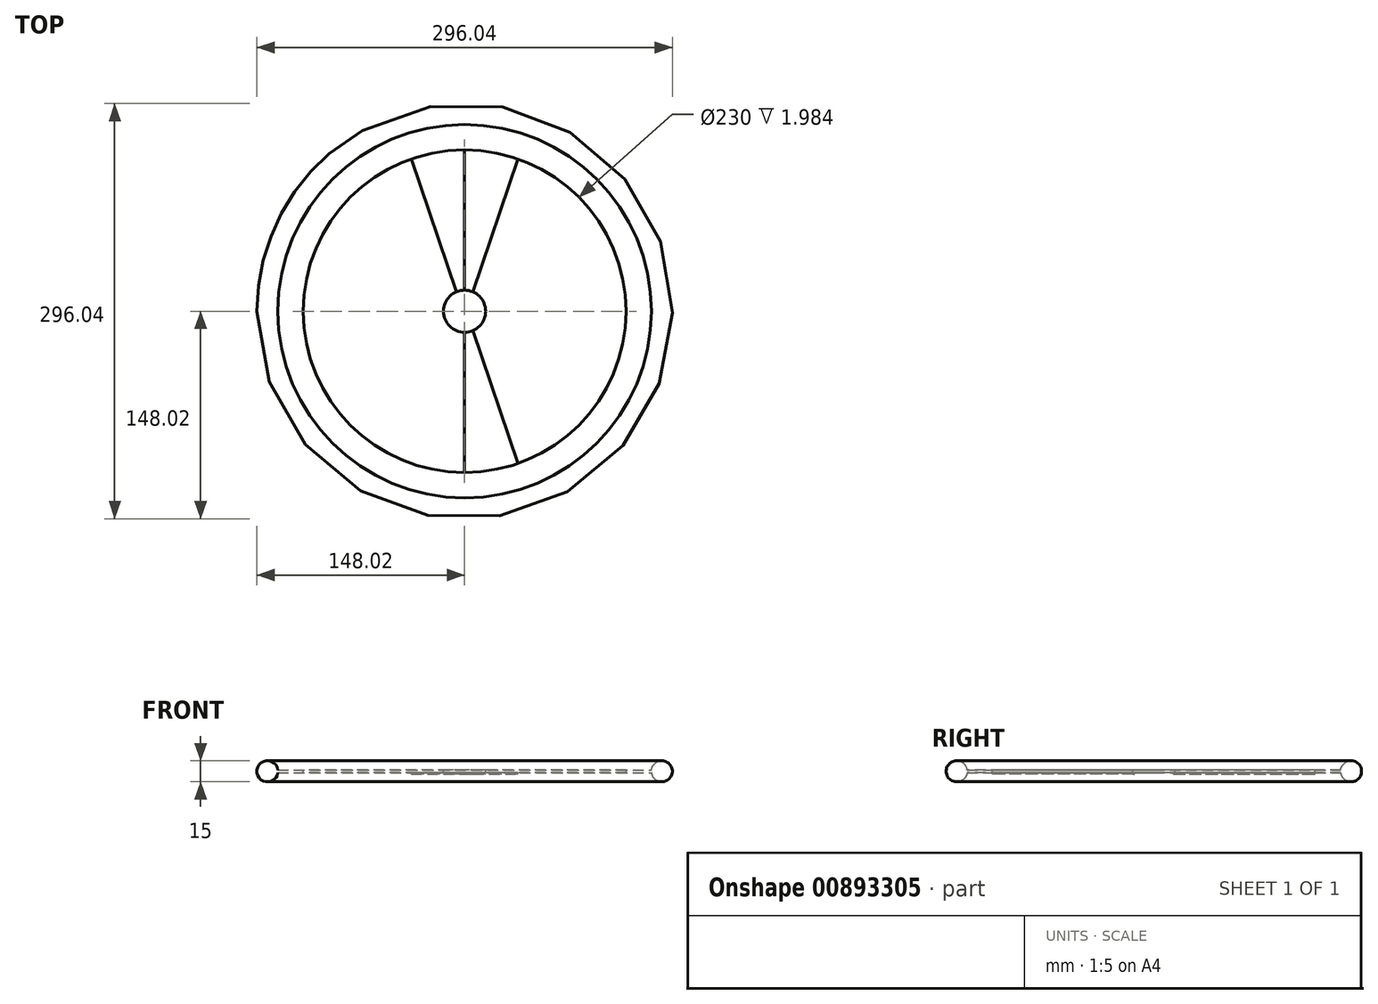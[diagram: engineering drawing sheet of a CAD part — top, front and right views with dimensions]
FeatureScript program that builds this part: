
annotation { "Feature Type Name" : "Feature", "Feature Type Description" : "" }
export const myFeature = defineFeature(function(context is Context, id is Id, definition is map)
    precondition{}
    {
        {
            var Q0;
            Q0=qCreatedBy(makeId("Front.planeOp"),FACE);
            var sketch = newSketch(context, id + "F0", { "sketchPlane" : qUnion([Q0])});
            skCircle(sketch, "E0", {"center": v(140.52, 0) * mm, "radius": 7.5 * mm});
            skPoint(sketch, "E1.0", {"position": v(0, 0) * mm});
            skLineSegment(sketch, "E2", {"start": v(0, 0) * mm, "end": v(140.52, 0) * mm});
            skLineSegment(sketch, "E3", {"start": v(0, 0) * mm, "end": v(0, 62.68) * mm});
            skLineSegment(sketch, "E4.bottom", {"start": v(140.52, -1) * mm, "end": v(0, -1) * mm});
            skLineSegment(sketch, "E4.top", {"start": v(140.52, 1) * mm, "end": v(0, 1) * mm});
            skLineSegment(sketch, "E4.left", {"start": v(140.52, -1) * mm, "end": v(140.52, 1) * mm});
            skLineSegment(sketch, "E4.right", {"start": v(0, -1) * mm, "end": v(0, 1) * mm});
            skPoint(sketch, "E4.middle", {"position": v(70.26, 0) * mm});
            skSolve(sketch);
        }
        {
            var Q0;
            Q0=makeQuery(id+"F0.imprint","IMPRINT",FACE,{"disambiguationData":[TD([[makeQuery(id+"F0.imprint","IMPRINT",EDGE,{"derivedFrom":sQuery(id+"F0.wireOp",EDGE,"E0")}),1.0]])]});
            var Q1;
            {var subQ4=sQuery(id+"F0.wireOp",EDGE,"E0");var subQ6=sQuery(id+"F0.wireOp",EDGE,"E4.top");var subQ8=makeQuery(id+"F0.imprint","INTERSECT",VERTEX,{"derivedFrom":[subQ4,subQ6]});Q1=makeQuery(id+"F0.imprint","IMPRINT",FACE,{"disambiguationData":[TD([[makeQuery(id+"F0.imprint","IMPRINT",EDGE,{"disambiguationData":[TD([[subQ8,1.0]])],"derivedFrom":subQ4}),1.0]])]});}
            var Q2;
            {var subQ0=sQuery(id+"F0.wireOp",EDGE,"E4.top");var subQ1=sQuery(id+"F0.wireOp",EDGE,"E0");var subQ2=makeQuery(id+"F0.imprint","INTERSECT",VERTEX,{"derivedFrom":[subQ1,subQ0]});Q2=makeQuery(id+"F0.imprint","IMPRINT",FACE,{"disambiguationData":[TD([[makeQuery(id+"F0.imprint","IMPRINT",EDGE,{"disambiguationData":[TD([[subQ2,-1.0]])],"derivedFrom":subQ1}),-1.0]])]});}
            var Q3;
            {var subQ0=sQuery(id+"F0.wireOp",EDGE,"E4.bottom");var subQ1=sQuery(id+"F0.wireOp",EDGE,"E0");var subQ2=makeQuery(id+"F0.imprint","INTERSECT",VERTEX,{"derivedFrom":[subQ1,subQ0]});Q3=makeQuery(id+"F0.imprint","IMPRINT",FACE,{"disambiguationData":[TD([[makeQuery(id+"F0.imprint","IMPRINT",EDGE,{"disambiguationData":[TD([[subQ2,1.0]])],"derivedFrom":subQ1}),-1.0]])]});}
            var Q4;
            Q4=sQuery(id+"F0.wireOp",EDGE,"E3");
            revolve(context, id + "F1", {"surfaceOperationType" : NewSurfaceOperationType.NEW, "entities" : qUnion([Q0, Q1, Q2, Q3]), "axis" : qUnion([Q4]), "revolveType" : RevolveType.FULL});
        }
        {
            var Q0;
            Q0=makeQuery(id+"F1.opRevolve","SWEPT_FACE",FACE,{"disambiguationData":[OSD([sQuery(id+"F0.wireOp",EDGE,"E4.top")])]});
            var sketch = newSketch(context, id + "F2", { "sketchPlane" : qUnion([Q0])});
            skCircle(sketch, "E5", {"center": v(0, 0) * mm, "radius": 115 * mm});
            skCircle(sketch, "E6", {"center": v(0, 0) * mm, "radius": 15 * mm});
            skLineSegment(sketch, "E7", {"start": v(-15, 0) * mm, "end": v(-15, -114.02) * mm});
            skLineSegment(sketch, "E8", {"start": v(15, 0) * mm, "end": v(15, -114.02) * mm});
            skSolve(sketch);
        }
        {
            var Q0;
            Q0=makeQuery(id+"F2.imprint","IMPRINT",FACE,{"disambiguationData":[TD([[makeQuery(id+"F2.imprint","IMPRINT",EDGE,{"derivedFrom":sQuery(id+"F2.wireOp",EDGE,"E5")}),1.0]])]});
            extrude(context, id + "F3", {"entities" : qUnion([Q0]), "operationType" : NewBodyOperationType.REMOVE, "oppositeDirection" : true, "depth" : 25 * mm, "offsetDistance" : 25 * mm});
        }
        {
            var Q0;
            Q0=makeQuery(id+"F3.boolean.opBoolean","SPLIT",FACE,{"disambiguationData":[TD([makeQuery(id+"F3.opExtrude","SWEPT_FACE",FACE,{"disambiguationData":[OSD([sQuery(id+"F2.wireOp",EDGE,"E6")])]})])],"derivedFrom":makeQuery(id+"F1.opRevolve","SWEPT_FACE",FACE,{"disambiguationData":[OSD([sQuery(id+"F0.wireOp",EDGE,"E4.bottom")])]})});
            var sketch = newSketch(context, id + "F4", { "sketchPlane" : qUnion([Q0])});
            skCircle(sketch, "E9.0", {"center": v(0, 0) * mm, "radius": 15 * mm});
            skCircle(sketch, "E10.0", {"center": v(0, 0) * mm, "radius": 115 * mm});
            skLineSegment(sketch, "E11", {"start": v(0, 15) * mm, "end": v(0, 115) * mm});
            skLineSegment(sketch, "E12", {"start": v(5.97, 13.76) * mm, "end": v(38.06, 108.52) * mm});
            skSolve(sketch);
        }
        {
            var Q0;
            {var subQ0=sQuery(id+"F4.wireOp",EDGE,"E11");Q0=makeQuery(id+"F4.imprint","IMPRINT",FACE,{"disambiguationData":[TD([[makeQuery(id+"F4.imprint","IMPRINT",EDGE,{"derivedFrom":subQ0}),-1.0]])]});}
            extrude(context, id + "F5", {"entities" : qUnion([Q0]), "depth" : 1 * mm, "offsetDistance" : 25 * mm});
        }
        {
            var Q0;
            Q0=makeQuery(id+"F5.opExtrude","SWEPT_BODY",BODY,{"disambiguationData":[OSD([sQuery(id+"F4.wireOp",EDGE,"E9.0"),sQuery(id+"F4.wireOp",EDGE,"E10.0"),sQuery(id+"F4.wireOp",EDGE,"E11"),sQuery(id+"F4.wireOp",EDGE,"E12")])]});
            var Q1;
            Q1=qCreatedBy(makeId("Front.planeOp"),FACE);
            mirror(context, id + "F6", {"entities" : qUnion([Q0]), "mirrorPlane" : qUnion([Q1])});
        }
        {
            var Q0;
            Q0=makeQuery(id+"F6.opPattern","COPY",BODY,{"derivedFrom":makeQuery(id+"F5.opExtrude","SWEPT_BODY",BODY,{"disambiguationData":[OSD([sQuery(id+"F4.wireOp",EDGE,"E9.0"),sQuery(id+"F4.wireOp",EDGE,"E10.0"),sQuery(id+"F4.wireOp",EDGE,"E11"),sQuery(id+"F4.wireOp",EDGE,"E12")])]}),"instanceName":"1"});
            var Q1;
            Q1=qCreatedBy(makeId("Right.planeOp"),FACE);
            mirror(context, id + "F7", {"operationType" : NewBodyOperationType.ADD, "entities" : qUnion([Q0]), "mirrorPlane" : qUnion([Q1])});
        }
    });
